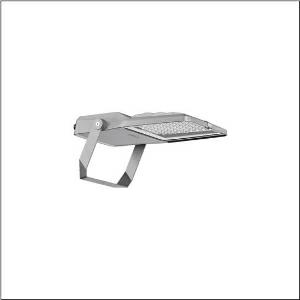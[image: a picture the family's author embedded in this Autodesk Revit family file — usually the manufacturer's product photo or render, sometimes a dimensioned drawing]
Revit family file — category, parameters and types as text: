
# Revit family: floodlight_fl_21_iq_mini___pl33t_5xa7771d4f1a_3e9c
name_source: partatom
category: Lighting Fixtures
units: mm (PartAtom-declared; Revit-internal decimal feet)

## family parameters
Cut with Voids When Loaded = No
Host = Face
Light Source = No
Part Type = Normal
Room Calculation Point = No
Round Connector Dimension = Use Diameter
Shared = No

## types (1)
- --- (1 x LED, 18390 lm, 143 W, 4000K)
    Apparent Load = 143 VA
    CIE Flux Codes = 26 75 99 100 100
    Color Rendering = 70
    Color Temperature = 4000K
    Default Elevation = 1800 mm
    Description = Floodlight FL 21 iQ mini, floodlight, primary light control with lens, of PMMA, primary optical cover: protective disc, of toughened safety glass, transparent, light distribution: PL33T, light emission: direct distribution, installation type: surface-mounted, LED, High Power LED, rated luminous flux: 18.390lm, luminous efficacy: 129lm/W, light colour: 740, colour temperature: 4000K, control gear: iQ Comfort/DALI, control: Auto-Match, Temp-Guard, Lumen-Switch, Night-Set, Smart-Wire, Light-Fading, Desk-Remote (wireless, voltage-free reading and setting of iQ features in the workshop via application-optimized NFC function/RFID function), optimised constant luminous flux control (CLO 2.0), with terminal, 6-pole, mains connection: 220..240V, AC, 50/60Hz, start of lifetime: 143W, end of service life: 152W, reduction: 61W, luminaire housing, of diecast aluminium, powder-coated, Siteco® metallic grey (DB 702S), corrosivity category C5 mid according to DIN EN ISO 12944, suitable for swimming pools, chlorine-resistant, sealing non-destructively replaceable, mounting bracket, of steel, galvanised, powder-coated, Siteco® metallic grey (DB 702S), protection rating (complete): IP66, insulation class (complete): insulation class II (safety insulation), certification: CE, ENEC, VDE, protection symbol: D, impact resistance: IK08, permissible operating ambient temperature: -40..+40°C, permissible operating ambient temperature for outdoor applications: -40..+50°C, standard: DIN EN 12944, LABS conformity tested according to VDMA 24364:2018-05, packaging unit: 1 piece

Light Distribution: PL33T
    Height = 70 mm
    Lamp = 1 x LED
    Lamp Light Flux = 18390 lm
    Lamp Power = 143 W
    Lamp count = 1
    Length = 485 mm
    Luminous efficacy = 129 lm/W
    Manufacturer = Siteco
    ModVariant = No
    Model = 5XA7771D4F1A
    Number of Poles = 1
    OnlyDefault = Yes
    Power Factor = 1
    Product Name = Floodlight FL 21 iQ mini | PL33T
    Product group = floodlight | pylon annexe
    ProductGroupID = 6201
    Protection Class = Protection class II
    Protection Degree = IP 66
    RLX_Detail_Level = 1
    RLX_Emergency_Light_Flux = 0 lm
    RLX_Emergency_Type = 0
    RLX_Emergency_Type_DB = No
    RlxData = <blob elided: 96645 chars, md5=bf055e68>
    Socket = socket
    Standby Power = 0 W
    System Light Flux = 18390 lm
    System Power = 143 W
    Type Comments = factory setting: luminous flux: 100 % | dim-lin: 254 | 730 mA
    Type Image = l_1006845.jpg
    URL = http://relux.com
    VarID = @adj_170601
    Voltage = 0 V
    Weight = 0.00 kg
    Width = 337 mm

## geometry (parser evidence)
native form markers: Blend x4, Sweep x14
no freeform markers — native parametric forms only
